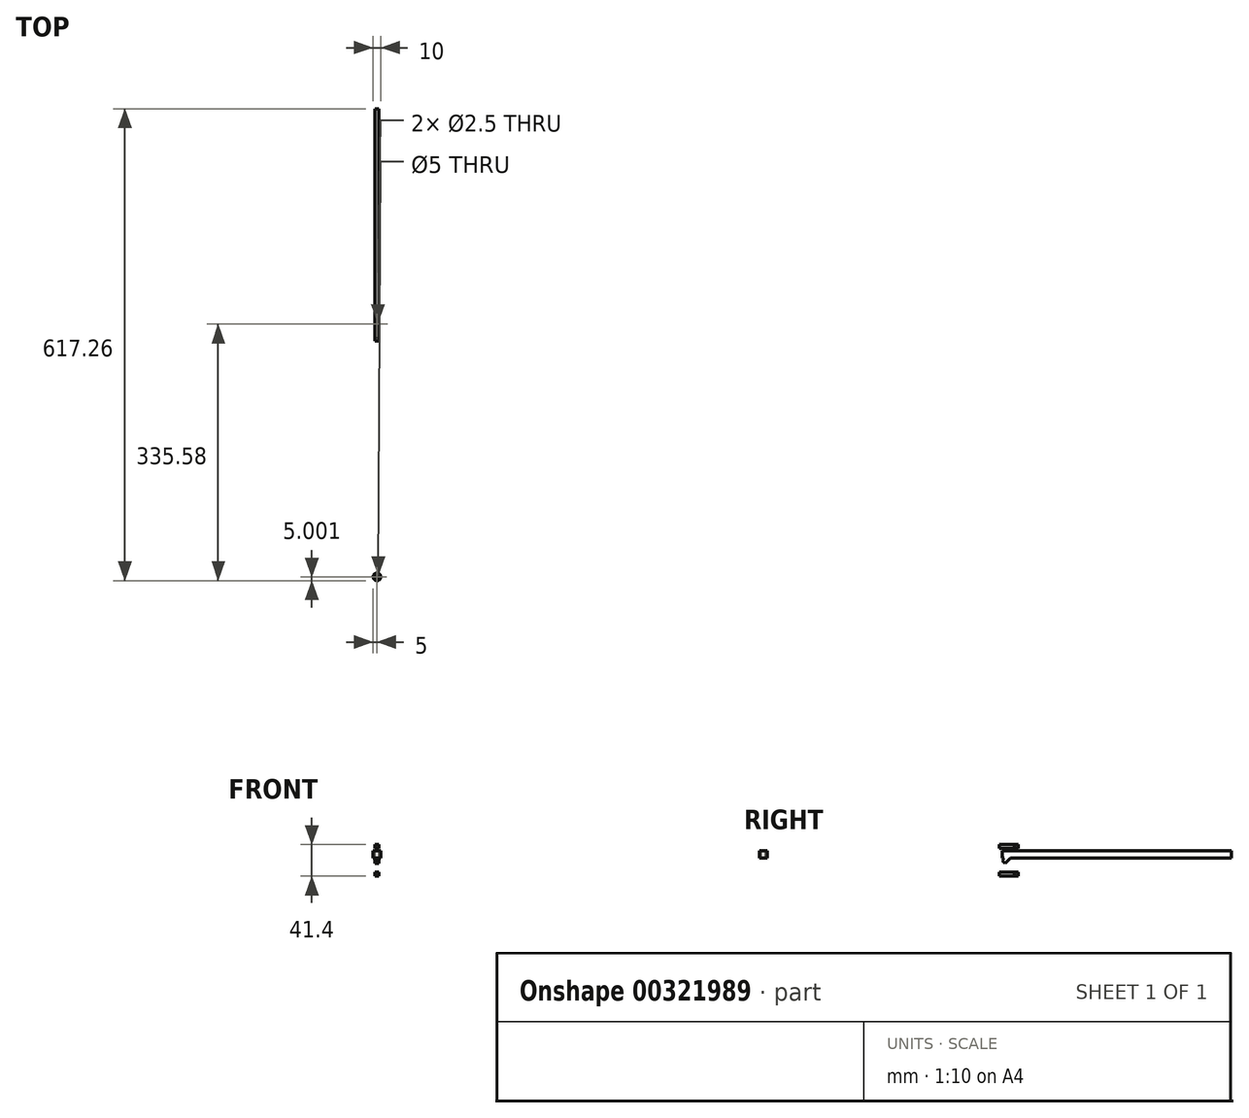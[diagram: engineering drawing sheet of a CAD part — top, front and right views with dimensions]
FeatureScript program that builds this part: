
annotation { "Feature Type Name" : "Feature", "Feature Type Description" : "" }
export const myFeature = defineFeature(function(context is Context, id is Id, definition is map)
    precondition{}
    {
        {
            var Q0;
            Q0=qCreatedBy(makeId("Top.planeOp"),FACE);
            var sketch = newSketch(context, id + "F0", { "sketchPlane" : qUnion([Q0])});
            skCircle(sketch, "E0", {"center": v(0, 0) * mm, "radius": 2.5 * mm});
            skCircle(sketch, "E1", {"center": v(0, 0) * mm, "radius": 1.25 * mm});
            skSolve(sketch);
        }
        {
            var Q0;
            Q0 = qSketchRegion(id + "F0", true);
            extrude(context, id + "F1", {"entities" : qUnion([Q0]), "depth" : 5 * mm});
        }
        {
            var Q0;
            Q0=qCreatedBy(makeId("Front.planeOp"),FACE);
            cPlane(context, id + "F2", {"entities" : qUnion([Q0]), "cplaneType" : CPlaneType.OFFSET, "offset" : 2 * mm, "width" : 150 * mm, "height" : 150 * mm});
        }
        {
            var Q0;
            Q0=qCreatedBy(id+"F2.planeOp",FACE);
            var sketch = newSketch(context, id + "F3", { "sketchPlane" : qUnion([Q0])});
            skLineSegment(sketch, "E2", {"start": v(0, 0) * mm, "end": v(0, 2.5) * mm, "construction": true});
            skLineSegment(sketch, "E3.bottom", {"start": v(2.5, 5) * mm, "end": v(-2.5, 5) * mm});
            skLineSegment(sketch, "E3.top", {"start": v(2.5, 0) * mm, "end": v(-2.5, 0) * mm});
            skLineSegment(sketch, "E3.left", {"start": v(2.5, 5) * mm, "end": v(2.5, 0) * mm});
            skLineSegment(sketch, "E3.right", {"start": v(-2.5, 5) * mm, "end": v(-2.5, 0) * mm});
            skPoint(sketch, "E3.middle", {"position": v(0, 2.5) * mm});
            skSolve(sketch);
        }
        {
            var Q0;
            Q0 = qSketchRegion(id + "F3", true);
            extrude(context, id + "F4", {"entities" : qUnion([Q0]), "operationType" : NewBodyOperationType.ADD, "depth" : 20 * mm});
        }
        {
            var Q0;
            Q0=makeQuery(id+"F4.opExtrude","CAP_EDGE",EDGE,{"disambiguationData":[OSD([sQuery(id+"F3.wireOp",EDGE,"E3.top")])],"isStart":false});
            cPlane(context, id + "F5", {"entities" : qUnion([Q0]), "cplaneType" : CPlaneType.LINE_ANGLE, "offset" : 25 * mm, "angle" : 135 * degree, "width" : 150 * mm, "height" : 150 * mm});
        }
        {
            var Q0;
            Q0=qCreatedBy(id+"F5.planeOp",FACE);
            var sketch = newSketch(context, id + "F6", { "sketchPlane" : qUnion([Q0])});
            skPoint(sketch, "E4", {"position": v(0, -8.49) * mm});
            skPoint(sketch, "E5", {"position": v(2.5, -8.49) * mm});
            skPoint(sketch, "E6", {"position": v(-2.5, -8.49) * mm});
            skLineSegment(sketch, "E7", {"start": v(-2.5, -8.49) * mm, "end": v(2.5, -8.49) * mm, "construction": true});
            skLineSegment(sketch, "E8.bottom", {"start": v(-2.5, -11.49) * mm, "end": v(2.5, -11.49) * mm});
            skLineSegment(sketch, "E8.top", {"start": v(-2.5, -5.49) * mm, "end": v(2.5, -5.49) * mm});
            skLineSegment(sketch, "E8.left", {"start": v(-2.5, -11.49) * mm, "end": v(-2.5, -5.49) * mm});
            skLineSegment(sketch, "E8.right", {"start": v(2.5, -11.49) * mm, "end": v(2.5, -5.49) * mm});
            skSolve(sketch);
        }
        {
            var Q0;
            Q0=makeQuery(id+"F6.imprint","IMPRINT",FACE,{"disambiguationData":[TD([[makeQuery(id+"F6.imprint","IMPRINT",EDGE,{"derivedFrom":sQuery(id+"F6.wireOp",EDGE,"E8.bottom")}),1.0]])]});
            extrude(context, id + "F7", {"entities" : qUnion([Q0]), "oppositeDirection" : true, "depth" : 8.48 * mm});
        }
        {
            var Q0;
            Q0=makeQuery(id+"F7.opExtrude","SWEPT_BODY",BODY,{"disambiguationData":[OSD([sQuery(id+"F6.wireOp",EDGE,"E8.bottom"),sQuery(id+"F6.wireOp",EDGE,"E8.top"),sQuery(id+"F6.wireOp",EDGE,"E8.left"),sQuery(id+"F6.wireOp",EDGE,"E8.right")])]});
            transform(context, id + "F8", {"entities" : qUnion([Q0]), "transformType" : TransformType.TRANSLATION_3D, "dx" : 0 * mm, "dy" : -5.2 * mm, "dz" : 5.18 * mm, "makeCopy" : false});
        }
        {
            var Q0;
            Q0=makeQuery(id+"F7.opExtrude","CAP_FACE",FACE,{"disambiguationData":[OSD([sQuery(id+"F6.wireOp",EDGE,"E8.bottom"),sQuery(id+"F6.wireOp",EDGE,"E8.top"),sQuery(id+"F6.wireOp",EDGE,"E8.left"),sQuery(id+"F6.wireOp",EDGE,"E8.right")])],"isStart":true});
            extrude(context, id + "F9", {"entities" : qUnion([Q0]), "operationType" : NewBodyOperationType.ADD, "depth" : 3.7 * mm});
        }
        {
            var Q0;
            Q0=makeQuery(id+"F7.opExtrude","CAP_EDGE",EDGE,{"disambiguationData":[OSD([sQuery(id+"F6.wireOp",EDGE,"E8.top")])],"isStart":false});
            cPlane(context, id + "F10", {"entities" : qUnion([Q0]), "cplaneType" : CPlaneType.LINE_ANGLE, "offset" : 25 * mm, "angle" : 90 * degree, "width" : 150 * mm, "height" : 150 * mm});
        }
        {
            var Q0;
            Q0=makeQuery(id+"F1.opExtrude","SWEPT_BODY",BODY,{"disambiguationData":[OSD([sQuery(id+"F0.wireOp",EDGE,"E0"),sQuery(id+"F0.wireOp",EDGE,"E1")])]});
            var Q1;
            Q1=qCreatedBy(id+"F10.planeOp",FACE);
            mirror(context, id + "F11", {"entities" : qUnion([Q0]), "mirrorPlane" : qUnion([Q1])});
        }
        {
            var Q0;
            Q0=makeQuery(id+"F7.opExtrude","CAP_EDGE",EDGE,{"disambiguationData":[OSD([sQuery(id+"F6.wireOp",EDGE,"E8.top")])],"isStart":false});
            cPlane(context, id + "F12", {"entities" : qUnion([Q0]), "cplaneType" : CPlaneType.LINE_ANGLE, "offset" : 25 * mm, "angle" : 0 * degree, "width" : 150 * mm, "height" : 150 * mm});
        }
        {
            var Q0;
            Q0=qCreatedBy(id+"F12.planeOp",FACE);
            var sketch = newSketch(context, id + "F13", { "sketchPlane" : qUnion([Q0])});
            skPoint(sketch, "E9", {"position": v(0, -7.94) * mm});
            skLineSegment(sketch, "E10.bottom", {"start": v(-2.5, -2.94) * mm, "end": v(2.5, -2.94) * mm});
            skLineSegment(sketch, "E10.top", {"start": v(-2.5, -12.94) * mm, "end": v(2.5, -12.94) * mm});
            skLineSegment(sketch, "E10.left", {"start": v(-2.5, -2.94) * mm, "end": v(-2.5, -12.94) * mm});
            skLineSegment(sketch, "E10.right", {"start": v(2.5, -2.94) * mm, "end": v(2.5, -12.94) * mm});
            skSolve(sketch);
        }
        {
            var Q0;
            Q0 = qSketchRegion(id + "F13", true);
            extrude(context, id + "F14", {"entities" : qUnion([Q0]), "operationType" : NewBodyOperationType.ADD, "oppositeDirection" : true, "depth" : 300 * mm});
        }
        {
            var Q0;
            Q0=makeQuery(id+"F14.opExtrude","SWEPT_FACE",FACE,{"disambiguationData":[OSD([sQuery(id+"F13.wireOp",EDGE,"E10.bottom")])]});
            var sketch = newSketch(context, id + "F15", { "sketchPlane" : qUnion([Q0])});
            skPoint(sketch, "E11", {"position": v(0, -326.08) * mm});
            skLineSegment(sketch, "E12", {"start": v(-0.34, -326.08) * mm, "end": v(0, -326.08) * mm, "construction": true});
            skLineSegment(sketch, "E13", {"start": v(0, -330.58) * mm, "end": v(0, -326.08) * mm, "construction": true});
            skCircle(sketch, "E14", {"center": v(0, -330.58) * mm, "radius": 5 * mm});
            skCircle(sketch, "E15", {"center": v(0, -330.58) * mm, "radius": 2.5 * mm});
            skSolve(sketch);
        }
        {
            var Q0;
            Q0 = qSketchRegion(id + "F15", true);
            extrude(context, id + "F16", {"entities" : qUnion([Q0]), "operationType" : NewBodyOperationType.ADD, "oppositeDirection" : true, "depth" : 10 * mm});
        }
    });
